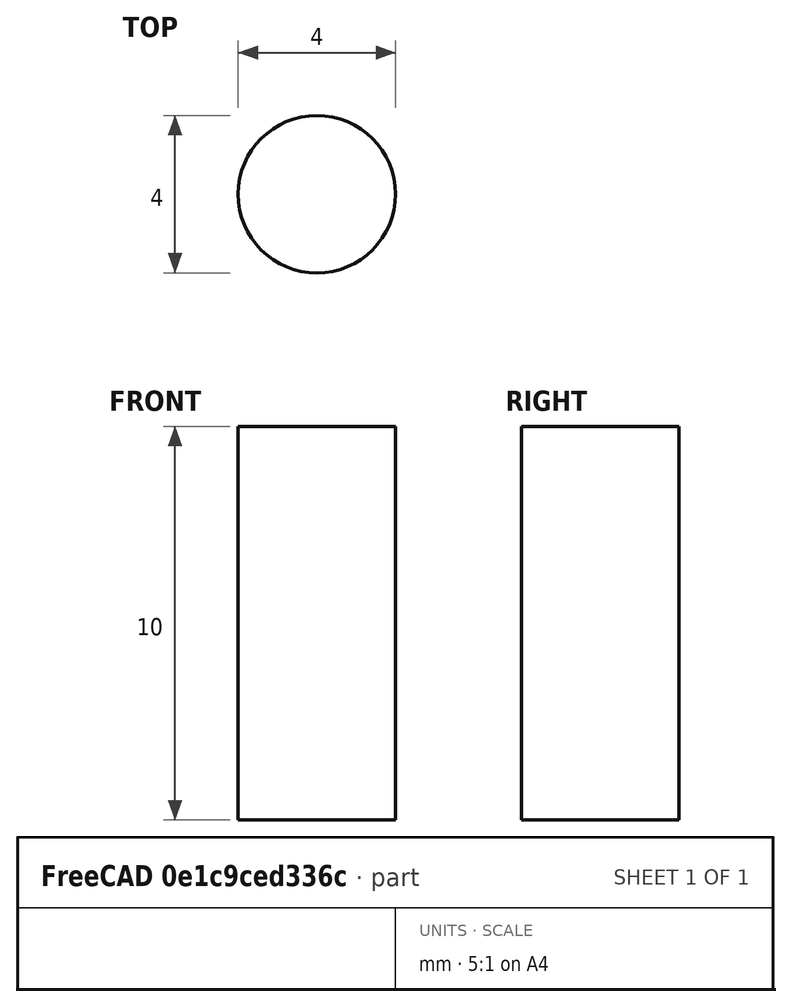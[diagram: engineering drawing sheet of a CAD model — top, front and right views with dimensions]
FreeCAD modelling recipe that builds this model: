
FCSTD DOCUMENT  (FreeCAD 0.17R12435 (Git))
Label: TestFoamKE
License: All rights reserved
LicenseURL: http://en.wikipedia.org/wiki/All_rights_reserved
objects: Fem::ConstraintFluidBoundary×2, Fem::FemSolverObjectPython×1, App::MaterialObjectPython×1, Fem::FeaturePython×1, Part::Cylinder×1, Fem::FemMeshObjectPython×1, Fem::FemAnalysisPython×1
note: 1 computed .brp shape members not serialized (recipe doc carries the construction recipe); baked Part::Feature solids carry a one-line shape summary decoded from their .brp

FEATURE [Fem::FemSolverObjectPython] OpenFOAM001  # FEM object (typed FeaturePython)
  Buoyant = false
  Compressible = false
  DynamicMeshing = false
  EndTime = 0
  Gravity = (0,0,0)
  HeatTransfering = false
  InputCaseName = TestCase
  NonNewtonian = false
  Parallel = false
  PhysicalDomain = 1
  Porous = false
  PotentialInit = false
  ResultObtained = true
  SolverName = OpenFOAM
  StartTime = 0
  TimeStep = 0
  Transient = false
  Transonic = false
  TurbulenceModel = 6
  WriteInterval = 0
FEATURE [App::MaterialObjectPython] FluidMaterial001  label="viscous_liquid"  # material (typed FeaturePython)
  Category = 1
  Material = Density=998.0 kg/m^3; Description=Standard distilled water properties at 20 Degrees Celsius and 1 atm; DynamicViscosity=1.003e-3 kg/m/s; KinematicViscosity=1000.0 m^2/s; MolarMass=18; Name=Water; SpecificHeat=4.18 J/kg/K; ThermalConductivity=0.59 W/m/K; ThermalExpansionCoefficient=0 um/m/K; VolumetricThermalExpansionCoefficient=2.07e-4 m/m/K
FEATURE [Fem::FeaturePython] MeshBoundaryLayer  # FEM object (typed FeaturePython)
  GrowthRate = 2
  MinimumThickness = 0.05
  NumberOfLayers = 4
FEATURE [Part::Cylinder] Cylinder
  Angle = 360
  AttacherType = Attacher::AttachEngine3D
  Height = 10
  Radius = 2
FEATURE [Fem::FemMeshObjectPython] Sweep_Mesh001  # FEM object (typed FeaturePython)
  Algorithm2D = 5
  Algorithm3D = 0
  CharacteristicLengthMax = 0.4
  CharacteristicLengthMin = 0
  CoherenceMesh = true
  ElementDimension = 0
  ElementOrder = 0
  GeometryTolerance = 1e-06
  HighOrderOptimize = false
  MeshBoundaryLayerList = -> [MeshBoundaryLayer]
  OptimizeNetgen = false
  OptimizeStd = false
  OutputFormat = 0
  Part = -> Cylinder
  RecombineAll = false
FEATURE [Fem::ConstraintFluidBoundary] FluidBoundary  label="inlet"
  BoundaryType = 0
  BoundaryValue = 0.01
  DirectionVector = (0,0,1)
  HTCoeffValue = 0
  HeatFluxValue = 0
  NormalDirection = (0,0,-1)
  Normals = (5) [(0,0,-1),(0,0,-1),(0,0,-1),(0,0,-1),(0,0,-1)]
  Points = (5) [(0,-2,0),(-2,0,0),(0,0,0),(2,0,0),(0,2,0)]
  References = -> [Cylinder]
  Reversed = true
  Subtype = 2
  TemperatureValue = 0
  ThermalBoundaryType = 1
  TurbulenceSpecification = 1
  TurbulentIntensityValue = 0.05
  TurbulentLengthValue = 0.02
FEATURE [Fem::ConstraintFluidBoundary] FluidBoundary001  label="outlet"
  BoundaryType = 2
  BoundaryValue = 100000
  DirectionVector = (0,0,1)
  HTCoeffValue = 0
  HeatFluxValue = 0
  NormalDirection = (0,0,1)
  Normals = (5) [(0,0,1),(0,0,1),(0,0,1),(0,0,1),(0,0,1)]
  Points = (5) [(0,-2,10),(-2,0,10),(0,0,10),(2,0,10),(0,2,10)]
  References = -> [Cylinder]
  Subtype = 1
  TemperatureValue = 0
  ThermalBoundaryType = 1
  TurbulenceSpecification = 1
  TurbulentIntensityValue = 0.05
  TurbulentLengthValue = 0.02
FEATURE [Fem::FemAnalysisPython] CfdAnalysis001  # FEM object (typed FeaturePython)
  Member = -> [OpenFOAM001,FluidMaterial001,Sweep_Mesh001,FluidBoundary,FluidBoundary001]
